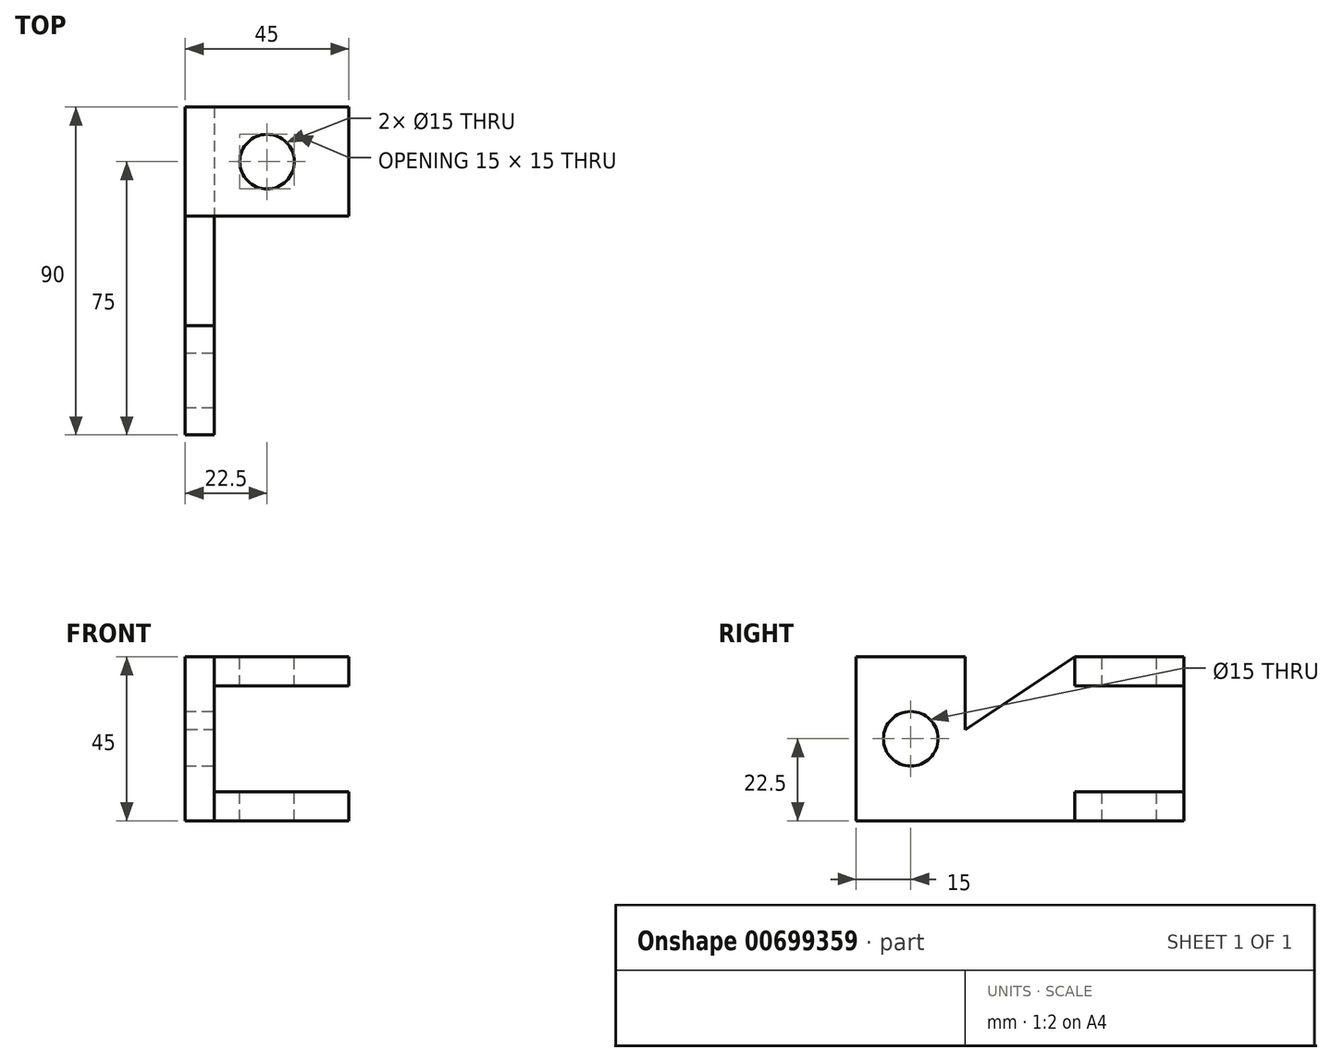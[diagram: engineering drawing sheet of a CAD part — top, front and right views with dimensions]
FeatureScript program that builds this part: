
annotation { "Feature Type Name" : "Feature", "Feature Type Description" : "" }
export const myFeature = defineFeature(function(context is Context, id is Id, definition is map)
    precondition{}
    {
        {
            var Q0;
            Q0=qCreatedBy(makeId("Right.planeOp"),FACE);
            var sketch = newSketch(context, id + "F0", { "sketchPlane" : qUnion([Q0])});
            skLineSegment(sketch, "E0.bottom", {"start": v(45, 22.5) * mm, "end": v(15, 22.5) * mm});
            skLineSegment(sketch, "E0.top", {"start": v(45, -22.5) * mm, "end": v(-45, -22.5) * mm});
            skLineSegment(sketch, "E0.left", {"start": v(45, 22.5) * mm, "end": v(45, -22.5) * mm});
            skLineSegment(sketch, "E0.right", {"start": v(-45, 22.5) * mm, "end": v(-45, -22.5) * mm});
            skPoint(sketch, "E0.middle", {"position": v(0, 0) * mm});
            skLineSegment(sketch, "E1", {"start": v(-15, 22.5) * mm, "end": v(-15, 2.5) * mm});
            skLineSegment(sketch, "E2", {"start": v(15, 22.5) * mm, "end": v(15, 2.5) * mm, "construction": true});
            skLineSegment(sketch, "E3.trimOffspring", {"start": v(-15, 22.5) * mm, "end": v(-45, 22.5) * mm});
            skLineSegment(sketch, "E4", {"start": v(-15, 2.5) * mm, "end": v(15, 22.5) * mm});
            skSolve(sketch);
        }
        {
            var Q0;
            Q0 = qSketchRegion(id + "F0", true);
            extrude(context, id + "F1", {"entities" : qUnion([Q0]), "depth" : 8 * mm, "offsetDistance" : 25 * mm});
        }
        {
            var Q0;
            Q0=makeQuery(id+"F1.opExtrude","CAP_FACE",FACE,{"disambiguationData":[OSD([sQuery(id+"F0.wireOp",EDGE,"E0.bottom"),sQuery(id+"F0.wireOp",EDGE,"E0.top"),sQuery(id+"F0.wireOp",EDGE,"E0.left"),sQuery(id+"F0.wireOp",EDGE,"E0.right"),sQuery(id+"F0.wireOp",EDGE,"E1"),sQuery(id+"F0.wireOp",EDGE,"E3.trimOffspring"),sQuery(id+"F0.wireOp",EDGE,"E4")])],"isStart":false});
            var sketch = newSketch(context, id + "F2", { "sketchPlane" : qUnion([Q0])});
            skLineSegment(sketch, "E5.bottom", {"start": v(45, 22.5) * mm, "end": v(15, 22.5) * mm});
            skLineSegment(sketch, "E5.top", {"start": v(45, 14.5) * mm, "end": v(15, 14.5) * mm});
            skLineSegment(sketch, "E5.left", {"start": v(45, 22.5) * mm, "end": v(45, 14.5) * mm});
            skLineSegment(sketch, "E5.right", {"start": v(15, 22.5) * mm, "end": v(15, 14.5) * mm});
            skLineSegment(sketch, "E6.bottom", {"start": v(45, -22.5) * mm, "end": v(15, -22.5) * mm});
            skLineSegment(sketch, "E6.top", {"start": v(45, -14.5) * mm, "end": v(15, -14.5) * mm});
            skLineSegment(sketch, "E6.left", {"start": v(45, -22.5) * mm, "end": v(45, -14.5) * mm});
            skLineSegment(sketch, "E6.right", {"start": v(15, -22.5) * mm, "end": v(15, -14.5) * mm});
            skSolve(sketch);
        }
        {
            var Q0;
            Q0=makeQuery(id+"F2.imprint","IMPRINT",FACE,{"disambiguationData":[TD([[makeQuery(id+"F2.imprint","IMPRINT",EDGE,{"derivedFrom":sQuery(id+"F2.wireOp",EDGE,"E5.bottom")}),1.0]])]});
            var Q1;
            Q1=makeQuery(id+"F2.imprint","IMPRINT",FACE,{"disambiguationData":[TD([[makeQuery(id+"F2.imprint","IMPRINT",EDGE,{"derivedFrom":sQuery(id+"F2.wireOp",EDGE,"E6.bottom")}),-1.0]])]});
            extrude(context, id + "F3", {"entities" : qUnion([Q0, Q1]), "operationType" : NewBodyOperationType.ADD, "depth" : 37 * mm, "offsetDistance" : 25 * mm});
        }
        {
            var Q0;
            Q0=makeQuery(id+"F3.boolean.opBoolean","MERGE",FACE,{"derivedFrom":[makeQuery(id+"F1.opExtrude","SWEPT_FACE",FACE,{"disambiguationData":[OSD([sQuery(id+"F0.wireOp",EDGE,"E0.bottom")])]}),makeQuery(id+"F3.opExtrude","SWEPT_FACE",FACE,{"disambiguationData":[OSD([sQuery(id+"F2.wireOp",EDGE,"E5.bottom")])]})]});
            var sketch = newSketch(context, id + "F4", { "sketchPlane" : qUnion([Q0])});
            skLineSegment(sketch, "E7", {"start": v(45, 30) * mm, "end": v(22.5, 30) * mm, "construction": true});
            skCircle(sketch, "E8", {"center": v(22.5, 30) * mm, "radius": 7.5 * mm});
            skSolve(sketch);
        }
        {
            var Q0;
            Q0 = qSketchRegion(id + "F4", true);
            extrude(context, id + "F5", {"entities" : qUnion([Q0]), "operationType" : NewBodyOperationType.REMOVE, "oppositeDirection" : true, "depth" : 45 * mm, "offsetDistance" : 25 * mm});
        }
        {
            var Q0;
            Q0=makeQuery(id+"F1.opExtrude","CAP_FACE",FACE,{"disambiguationData":[OSD([sQuery(id+"F0.wireOp",EDGE,"E0.bottom"),sQuery(id+"F0.wireOp",EDGE,"E0.top"),sQuery(id+"F0.wireOp",EDGE,"E0.left"),sQuery(id+"F0.wireOp",EDGE,"E0.right"),sQuery(id+"F0.wireOp",EDGE,"E1"),sQuery(id+"F0.wireOp",EDGE,"E3.trimOffspring"),sQuery(id+"F0.wireOp",EDGE,"E4")])],"isStart":false});
            var sketch = newSketch(context, id + "F6", { "sketchPlane" : qUnion([Q0])});
            skLineSegment(sketch, "E9", {"start": v(-30, 22.5) * mm, "end": v(-30, 0) * mm, "construction": true});
            skCircle(sketch, "E10", {"center": v(-30, 0) * mm, "radius": 7.5 * mm});
            skSolve(sketch);
        }
        {
            var Q0;
            Q0 = qSketchRegion(id + "F6", true);
            extrude(context, id + "F7", {"entities" : qUnion([Q0]), "operationType" : NewBodyOperationType.REMOVE, "oppositeDirection" : true, "depth" : 25 * mm, "offsetDistance" : 25 * mm});
        }
    });
